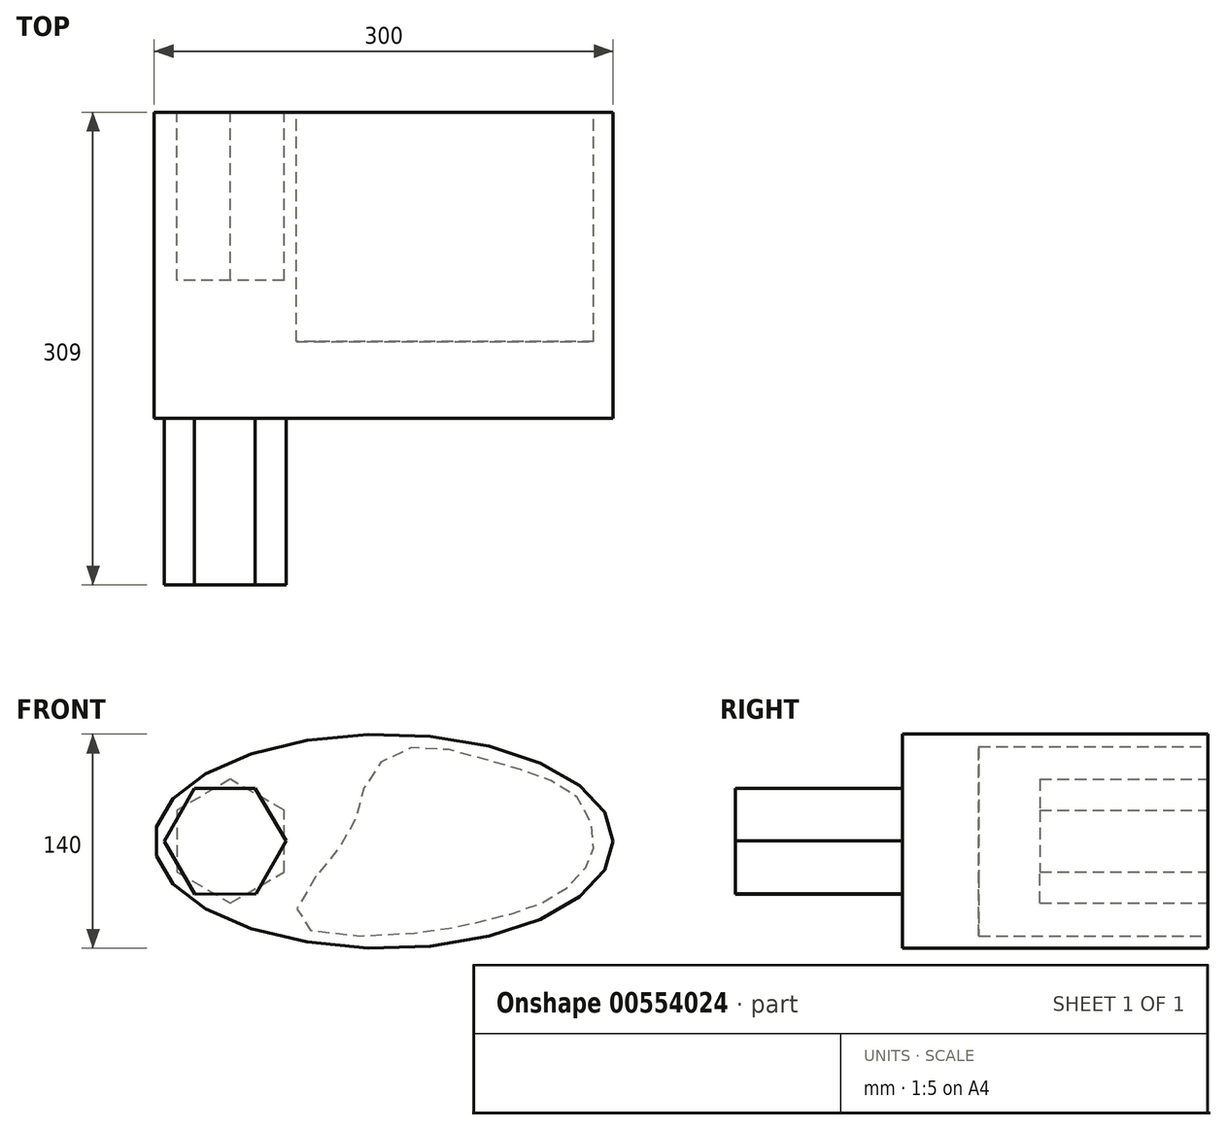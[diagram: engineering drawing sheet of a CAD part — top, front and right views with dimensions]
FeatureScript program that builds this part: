
annotation { "Feature Type Name" : "Feature", "Feature Type Description" : "" }
export const myFeature = defineFeature(function(context is Context, id is Id, definition is map)
    precondition{}
    {
        {
            var Q0;
            Q0=qCreatedBy(makeId("Front.planeOp"),FACE);
            var sketch = newSketch(context, id + "F0", { "sketchPlane" : qUnion([Q0])});
            skEllipse(sketch, "E0", {"center": v(0, 0) * mm, "majorRadius": 150 * mm, "minorRadius": 70 * mm, "majorAxis": v(1, 0)});
            skSolve(sketch);
        }
        {
            var Q0;
            Q0 = qSketchRegion(id + "F0", true);
            extrude(context, id + "F1", {"entities" : qUnion([Q0]), "depth" : 200 * mm, "offsetDistance" : 25.4 * mm});
        }
        {
            var Q0;
            Q0=makeQuery(id+"F1.opExtrude","CAP_FACE",FACE,{"disambiguationData":[OSD([sQuery(id+"F0.wireOp",EDGE,"E0")])],"isStart":false});
            var sketch = newSketch(context, id + "F2", { "sketchPlane" : qUnion([Q0])});
            skPoint(sketch, "E1.cCircle.perimeterSnap0", {"position": v(-150, 0) * mm});
            skPoint(sketch, "E1.0.midPoint", {"position": v(-124.9, 0) * mm});
            skPoint(sketch, "E1.0.midPoint.positionSnap0", {"position": v(-150, 0) * mm});
            skCircle(sketch, "E2.cCircle", {"center": v(-103.67, 0) * mm, "radius": 34.5 * mm, "construction": true});
            skLineSegment(sketch, "E2.0", {"start": v(-63.83, 0.25) * mm, "end": v(-83.53, -34.37) * mm});
            skLineSegment(sketch, "E2.1", {"start": v(-83.53, -34.37) * mm, "end": v(-123.37, -34.62) * mm});
            skLineSegment(sketch, "E2.2", {"start": v(-123.37, -34.62) * mm, "end": v(-143.5, -0.25) * mm});
            skLineSegment(sketch, "E2.3", {"start": v(-143.5, -0.25) * mm, "end": v(-123.8, 34.37) * mm});
            skLineSegment(sketch, "E2.4", {"start": v(-123.8, 34.37) * mm, "end": v(-83.97, 34.62) * mm});
            skLineSegment(sketch, "E2.5", {"start": v(-83.97, 34.62) * mm, "end": v(-63.83, 0.25) * mm});
            skPoint(sketch, "E2.0.midPoint", {"position": v(-73.68, -17.06) * mm});
            skSolve(sketch);
        }
        {
            var Q0;
            Q0 = qSketchRegion(id + "F2", true);
            extrude(context, id + "F3", {"entities" : qUnion([Q0]), "operationType" : NewBodyOperationType.ADD, "depth" : 109 * mm, "offsetDistance" : 25.4 * mm});
        }
        {
            var Q0;
            Q0=makeQuery(id+"F1.opExtrude","CAP_FACE",FACE,{"disambiguationData":[OSD([sQuery(id+"F0.wireOp",EDGE,"E0")])],"isStart":true});
            var sketch = newSketch(context, id + "F4", { "sketchPlane" : qUnion([Q0])});
            skCircle(sketch, "E3.cCircle", {"center": v(100.16, 0) * mm, "radius": 35 * mm, "construction": true});
            skLineSegment(sketch, "E3.0", {"start": v(135.16, 20.2) * mm, "end": v(135.16, -20.2) * mm});
            skLineSegment(sketch, "E3.1", {"start": v(135.16, -20.2) * mm, "end": v(100.16, -40.41) * mm});
            skLineSegment(sketch, "E3.2", {"start": v(100.16, -40.41) * mm, "end": v(65.16, -20.2) * mm});
            skLineSegment(sketch, "E3.3", {"start": v(65.16, -20.2) * mm, "end": v(65.16, 20.2) * mm});
            skLineSegment(sketch, "E3.4", {"start": v(65.16, 20.2) * mm, "end": v(100.16, 40.41) * mm});
            skLineSegment(sketch, "E3.5", {"start": v(100.16, 40.41) * mm, "end": v(135.16, 20.2) * mm});
            skPoint(sketch, "E3.0.midPoint", {"position": v(135.16, 0) * mm});
            skSolve(sketch);
        }
        {
            var Q0;
            Q0 = qSketchRegion(id + "F4", true);
            extrude(context, id + "F5", {"entities" : qUnion([Q0]), "operationType" : NewBodyOperationType.REMOVE, "oppositeDirection" : true, "depth" : 110 * mm, "offsetDistance" : 25.4 * mm});
        }
        {
            var Q0;
            Q0=makeQuery(id+"F1.opExtrude","CAP_FACE",FACE,{"disambiguationData":[OSD([sQuery(id+"F0.wireOp",EDGE,"E0")])],"isStart":true});
            var sketch = newSketch(context, id + "F6", { "sketchPlane" : qUnion([Q0])});
            skFitSpline(sketch, "E4", {"points": [v(44.35, -23.1) * mm, v(55.05, -54) * mm, v(-20.89, -59.88) * mm, v(-53.8, -54.66) * mm, v(-90.22, -45.38) * mm, v(-118.33, -31.64) * mm, v(-134.36, -13.71) * mm, v(-137.35, 0) * mm, v(-129.89, 24.72) * mm, v(-103.46, 42) * mm, v(-66.5, 53.35) * mm, v(-19.23, 61.24) * mm, v(9.77, 42.17) * mm, v(19.32, 11.67) * mm, v(44.35, -23.1) * mm]});
            skSolve(sketch);
        }
        {
            var Q0;
            Q0 = qSketchRegion(id + "F6", true);
            extrude(context, id + "F7", {"entities" : qUnion([Q0]), "operationType" : NewBodyOperationType.REMOVE, "oppositeDirection" : true, "depth" : 150 * mm, "offsetDistance" : 25.4 * mm});
        }
    });
